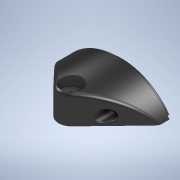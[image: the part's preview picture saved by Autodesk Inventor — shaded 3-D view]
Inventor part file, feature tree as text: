
AUTODESK INVENTOR PART (.ipt)
format: ipt  version: 2020 (Build 240168000, 168)  size: 304,128 bytes
history: native  units: in
note: dims shown in document units (in); Inventor stores cm internally (conversion verified against a paired STEP export)
features: sketch x6, extrude x3, hole x3, revolve x2, fillet x2, plane x1
ambient origin geometry x8: Origin, YZ Plane, XZ Plane, XY Plane, X Axis, Y Axis, Z Axis, Center Point
bodies: Solid1 (feature_tree)
feature tree (17):
  sketch  "Sketch1"  dims[d0=1.85in d1=0.125in]
  revolve  "Revolution1"  [1 undecoded]
  extrude  "Extrusion1"  Depth=0.25in
  extrude  "Extrusion2"  Depth=1.375in
  hole  "Hole1"  [1 undecoded]
  plane  "Work Plane1"
  hole  "Hole2"  [1 undecoded]
  extrude  "Extrusion4"  Depth=3.25in
  revolve  "Revolution2"  [1 undecoded]
  hole  "Hole4"  [1 undecoded]
  fillet  "Fillet1"  [1 undecoded]
  fillet  "Fillet2"  Radius=1.2in
  sketch  "Sketch2"  dims[d2=1.74in d3=0.25in]
  sketch  "Sketch3"  dims[d4=0.25in d5=1.375in]
  sketch  "Sketch5"  dims[d6=180.0deg d7=1.0in d8=0.0in]
  sketch  "Sketch8"  dims[d9=1.332in d10=0.0in d11=1.5in]
  sketch  "Sketch9"  dims[d12=1.25in d13=0.205in d14=0.75in d15=0.3438in d16=1.0in d17=0.5635in d18=1.0in d19=0.8108in d20=0.266in d21=0.75in d22=0.625in d23=0.313in d24=0.5635in d25=1.0in d26=0.8108in d30=3.25in d31=1.0in d32=0.5in d33=0.0in d45=120.0deg d49=1.2in d50=180.0deg d52=0.325in d53=0.5in d54=0.5625in d55=0.35in d56=0.75in d57=0.51in d58=0.188in d59=0.5635in d60=0.25in d61=0.0in d62=0.125in d63=0.0312in d38=1.0in d39=1.0in d40=1.0in d41=0.15in d42=0.25in d43=0.375in d44=0.5635in d46=0.8108in d47=0.0625in d48=0.75in]
note: 6 required parameter values undecoded (feature->parameter linkage not recoverable at this tier; creation-order binding heuristic only, values carry confidence <= 0.55)